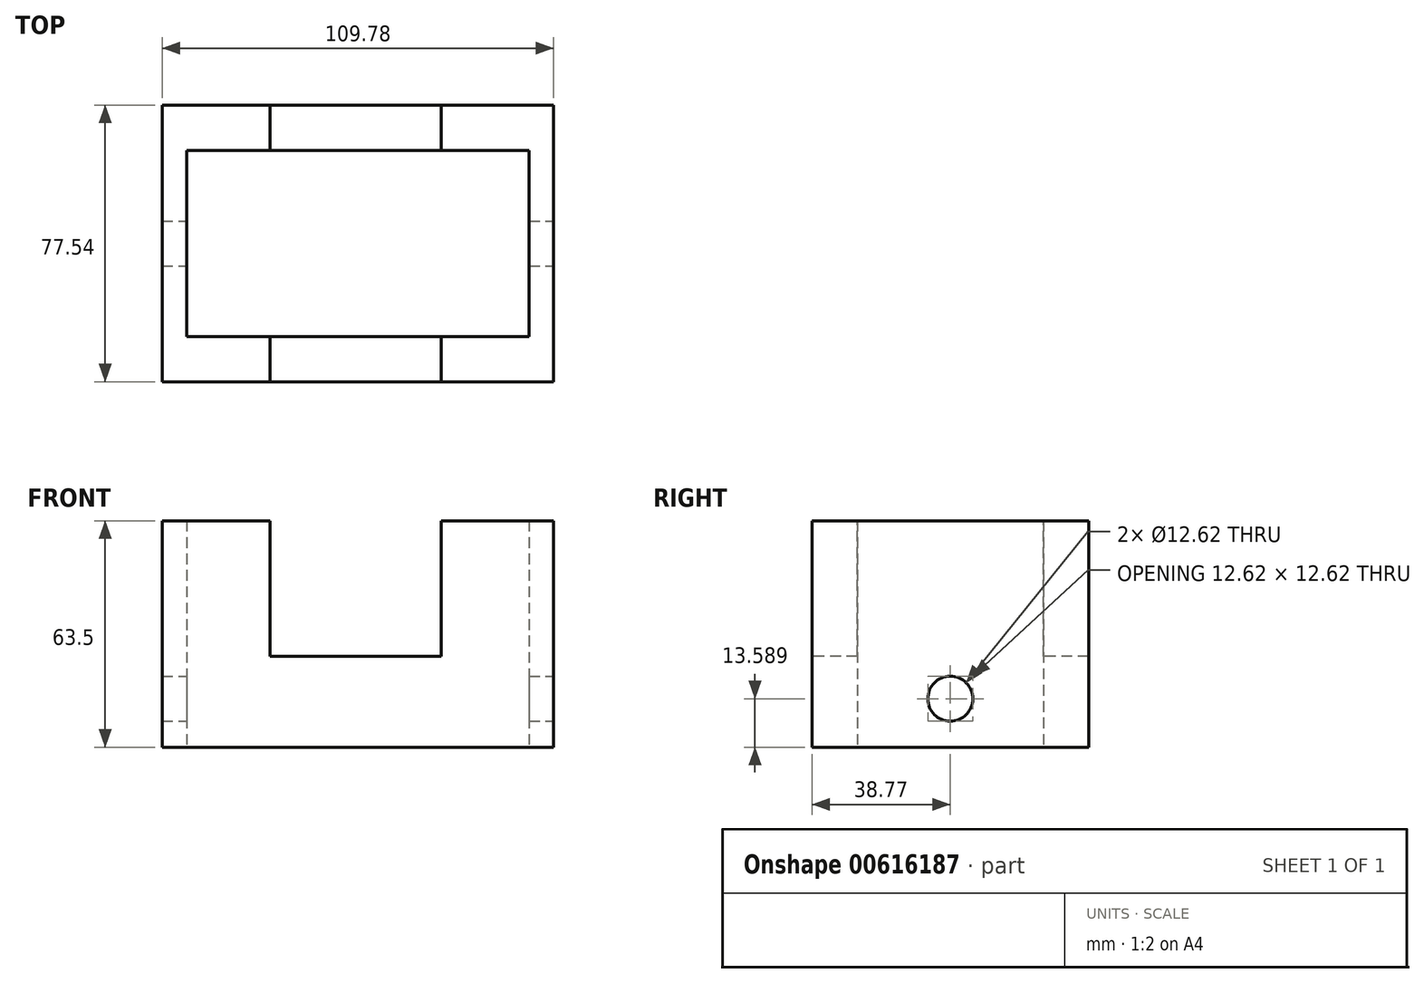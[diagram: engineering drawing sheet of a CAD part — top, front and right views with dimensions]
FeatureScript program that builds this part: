
annotation { "Feature Type Name" : "Feature", "Feature Type Description" : "" }
export const myFeature = defineFeature(function(context is Context, id is Id, definition is map)
    precondition{}
    {
        {
            var Q0;
            Q0=qCreatedBy(makeId("Top.planeOp"),FACE);
            var sketch = newSketch(context, id + "F0", { "sketchPlane" : qUnion([Q0])});
            skLineSegment(sketch, "E0.bottom", {"start": v(-54.89, 38.77) * mm, "end": v(54.89, 38.77) * mm});
            skLineSegment(sketch, "E0.top", {"start": v(-54.89, -38.77) * mm, "end": v(54.89, -38.77) * mm});
            skLineSegment(sketch, "E0.left", {"start": v(-54.89, 38.77) * mm, "end": v(-54.89, -38.77) * mm});
            skLineSegment(sketch, "E0.right", {"start": v(54.89, 38.77) * mm, "end": v(54.89, -38.77) * mm});
            skPoint(sketch, "E0.middle", {"position": v(0, 0) * mm});
            skSolve(sketch);
        }
        {
            var Q0;
            Q0 = qSketchRegion(id + "F0", true);
            extrude(context, id + "F1", {"entities" : qUnion([Q0]), "depth" : 63.5 * mm, "offsetDistance" : 25.4 * mm});
        }
        {
            var Q0;
            Q0=qCreatedBy(makeId("Top.planeOp"),FACE);
            var sketch = newSketch(context, id + "F2", { "sketchPlane" : qUnion([Q0])});
            skLineSegment(sketch, "E1.bottom", {"start": v(-48.03, -26.09) * mm, "end": v(48.03, -26.09) * mm});
            skLineSegment(sketch, "E1.top", {"start": v(-48.03, 26.09) * mm, "end": v(48.03, 26.09) * mm});
            skLineSegment(sketch, "E1.left", {"start": v(-48.03, -26.09) * mm, "end": v(-48.03, 26.09) * mm});
            skLineSegment(sketch, "E1.right", {"start": v(48.03, -26.09) * mm, "end": v(48.03, 26.09) * mm});
            skPoint(sketch, "E1.middle", {"position": v(0, 0) * mm});
            skSolve(sketch);
        }
        {
            var Q0;
            Q0 = qSketchRegion(id + "F2", true);
            extrude(context, id + "F3", {"entities" : qUnion([Q0]), "operationType" : NewBodyOperationType.REMOVE, "oppositeDirection" : true, "depth" : -63.5 * mm, "offsetDistance" : 25.4 * mm});
        }
        {
            var Q0;
            Q0=qCreatedBy(makeId("Top.planeOp"),FACE);
            var sketch = newSketch(context, id + "F4", { "sketchPlane" : qUnion([Q0])});
            skLineSegment(sketch, "E2.bottom", {"start": v(-40.9, -31.8) * mm, "end": v(40.9, -31.8) * mm});
            skLineSegment(sketch, "E2.top", {"start": v(-40.9, 31.8) * mm, "end": v(40.9, 31.8) * mm});
            skLineSegment(sketch, "E2.left", {"start": v(-40.9, -31.8) * mm, "end": v(-40.9, 31.8) * mm});
            skLineSegment(sketch, "E2.right", {"start": v(40.9, -31.8) * mm, "end": v(40.9, 31.8) * mm});
            skPoint(sketch, "E2.middle", {"position": v(0, 0) * mm});
            skSolve(sketch);
        }
        {
            var Q0;
            Q0 = qSketchRegion(id + "F4", true);
            extrude(context, id + "F5", {"entities" : qUnion([Q0]), "operationType" : NewBodyOperationType.REMOVE, "oppositeDirection" : true, "depth" : 63.5 * mm, "offsetDistance" : 25.4 * mm});
        }
        {
            var Q0;
            Q0=makeQuery(id+"F1.opExtrude","SWEPT_FACE",FACE,{"disambiguationData":[OSD([sQuery(id+"F0.wireOp",EDGE,"E0.top")])]});
            var sketch = newSketch(context, id + "F6", { "sketchPlane" : qUnion([Q0])});
            skLineSegment(sketch, "E3", {"start": v(-24.58, 63.5) * mm, "end": v(-24.58, 25.5) * mm});
            skLineSegment(sketch, "E4", {"start": v(-24.58, 25.5) * mm, "end": v(23.36, 25.5) * mm});
            skLineSegment(sketch, "E5", {"start": v(23.36, 25.5) * mm, "end": v(23.36, 63.5) * mm});
            skLineSegment(sketch, "E6", {"start": v(23.36, 63.5) * mm, "end": v(-24.58, 63.5) * mm});
            skSolve(sketch);
        }
        {
            var Q0;
            Q0 = qSketchRegion(id + "F6", true);
            extrude(context, id + "F7", {"entities" : qUnion([Q0]), "operationType" : NewBodyOperationType.REMOVE, "oppositeDirection" : true, "depth" : 101.6 * mm, "offsetDistance" : 25.4 * mm});
        }
        {
            var Q0;
            Q0=makeQuery(id+"F1.opExtrude","SWEPT_FACE",FACE,{"disambiguationData":[OSD([sQuery(id+"F0.wireOp",EDGE,"E0.right")])]});
            var sketch = newSketch(context, id + "F8", { "sketchPlane" : qUnion([Q0])});
            skCircle(sketch, "E7", {"center": v(0, 13.59) * mm, "radius": 6.31 * mm});
            skSolve(sketch);
        }
        {
            var Q0;
            Q0 = qSketchRegion(id + "F8", true);
            extrude(context, id + "F9", {"entities" : qUnion([Q0]), "operationType" : NewBodyOperationType.REMOVE, "oppositeDirection" : true, "depth" : 254 * mm, "offsetDistance" : 25.4 * mm});
        }
    });
